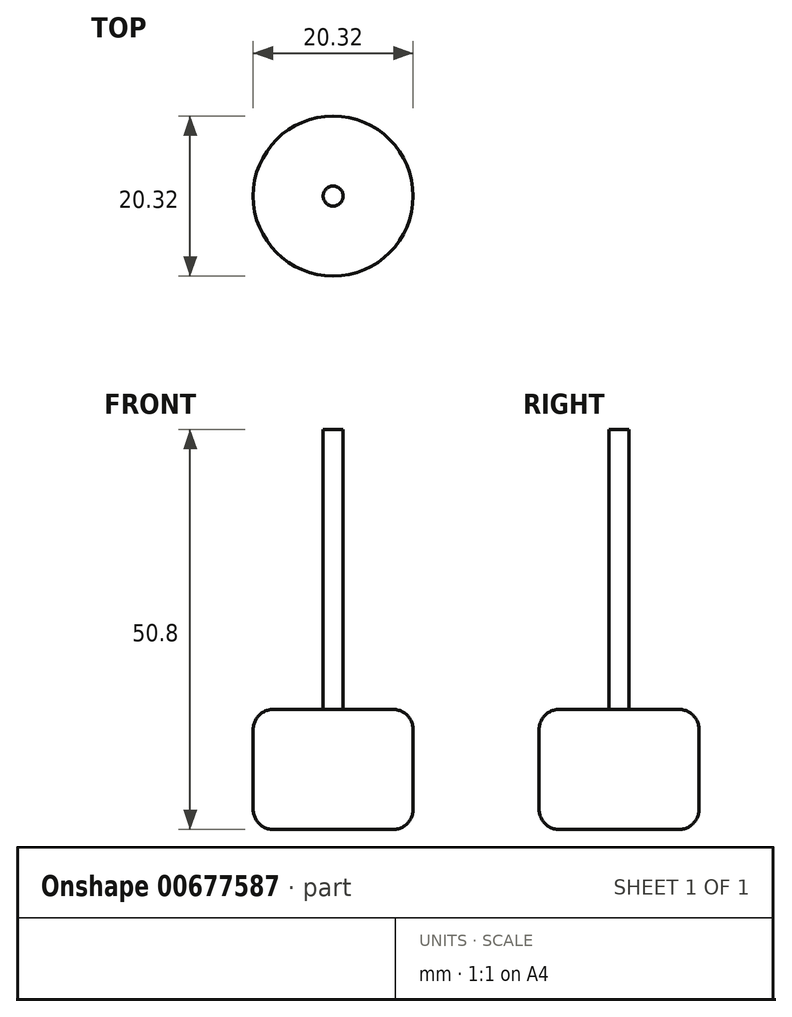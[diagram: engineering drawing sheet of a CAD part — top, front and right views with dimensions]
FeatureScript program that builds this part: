
annotation { "Feature Type Name" : "Feature", "Feature Type Description" : "" }
export const myFeature = defineFeature(function(context is Context, id is Id, definition is map)
    precondition{}
    {
        {
            var Q0;
            Q0=qCreatedBy(makeId("Top.planeOp"),FACE);
            var sketch = newSketch(context, id + "F0", { "sketchPlane" : qUnion([Q0])});
            skCircle(sketch, "E0", {"center": v(0, 0) * mm, "radius": 10.16 * mm});
            skSolve(sketch);
        }
        {
            var Q0;
            Q0=makeQuery(id+"F0.imprint","IMPRINT",FACE,{"disambiguationData":[TD([[makeQuery(id+"F0.imprint","IMPRINT",EDGE,{"derivedFrom":sQuery(id+"F0.wireOp",EDGE,"E0")}),1.0]])]});
            extrude(context, id + "F1", {"entities" : qUnion([Q0]), "depth" : 15.24 * mm, "offsetDistance" : 25.4 * mm});
        }
        {
            var Q0;
            Q0=makeQuery(id+"F1.opExtrude","CAP_EDGE",EDGE,{"disambiguationData":[OSD([sQuery(id+"F0.wireOp",EDGE,"E0")])],"isStart":false});
            var Q1;
            Q1=makeQuery(id+"F1.opExtrude","CAP_EDGE",EDGE,{"disambiguationData":[OSD([sQuery(id+"F0.wireOp",EDGE,"E0")])],"isStart":true});
            fillet(context, id + "F2", {"entities" : qUnion([Q0, Q1]), "radius" : 2.54 * mm, "tangentPropagation" : true, "allowEdgeOverflow" : false});
        }
        {
            var Q0;
            Q0=makeQuery(id+"F1.opExtrude","CAP_FACE",FACE,{"disambiguationData":[OSD([sQuery(id+"F0.wireOp",EDGE,"E0")])],"isStart":false});
            var sketch = newSketch(context, id + "F3", { "sketchPlane" : qUnion([Q0])});
            skCircle(sketch, "E1", {"center": v(0, 0) * mm, "radius": 1.27 * mm});
            skSolve(sketch);
        }
        {
            var Q0;
            Q0=qSketchRegion(id+"F3",true);
            extrude(context, id + "F4", {"entities" : qUnion([Q0]), "operationType" : NewBodyOperationType.ADD, "depth" : 35.56 * mm, "offsetDistance" : 25.4 * mm});
        }
    });
